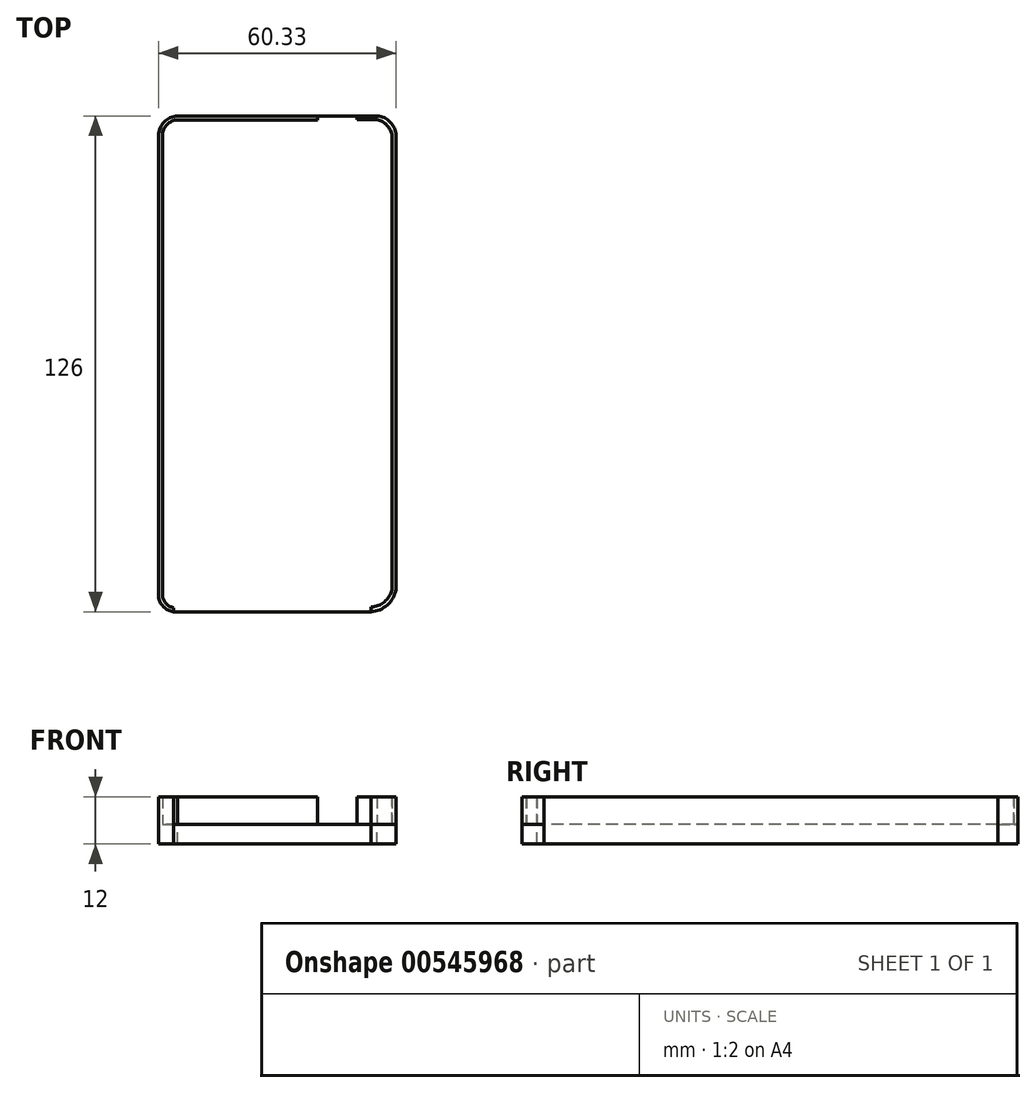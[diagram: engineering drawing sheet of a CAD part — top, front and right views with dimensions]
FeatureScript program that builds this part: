
annotation { "Feature Type Name" : "Feature", "Feature Type Description" : "" }
export const myFeature = defineFeature(function(context is Context, id is Id, definition is map)
    precondition{}
    {
        {
            var Q0;
            Q0=qCreatedBy(makeId("Top.planeOp"),FACE);
            var sketch = newSketch(context, id + "F0", { "sketchPlane" : qUnion([Q0])});
            skLineSegment(sketch, "E0.bottom", {"start": v(-22.18, 65.1) * mm, "end": v(38.15, 65.1) * mm});
            skLineSegment(sketch, "E0.top", {"start": v(-22.18, -60.9) * mm, "end": v(38.15, -60.9) * mm});
            skLineSegment(sketch, "E0.left", {"start": v(-22.18, 65.1) * mm, "end": v(-22.18, -60.9) * mm});
            skLineSegment(sketch, "E0.right", {"start": v(38.15, 65.1) * mm, "end": v(38.15, -60.9) * mm});
            skSolve(sketch);
        }
        {
            var Q0;
            Q0=makeQuery(id+"F0.imprint","IMPRINT",FACE,{"disambiguationData":[TD([[makeQuery(id+"F0.imprint","IMPRINT",EDGE,{"derivedFrom":sQuery(id+"F0.wireOp",EDGE,"E0.bottom")}),-1.0]])]});
            extrude(context, id + "F1", {"entities" : qUnion([Q0]), "depth" : 5 * mm, "offsetDistance" : 25 * mm});
        }
        {
            var Q0;
            Q0=makeQuery(id+"F1.opExtrude","CAP_FACE",FACE,{"disambiguationData":[OSD([sQuery(id+"F0.wireOp",EDGE,"E0.bottom"),sQuery(id+"F0.wireOp",EDGE,"E0.top"),sQuery(id+"F0.wireOp",EDGE,"E0.left"),sQuery(id+"F0.wireOp",EDGE,"E0.right")])],"isStart":false});
            var sketch = newSketch(context, id + "F2", { "sketchPlane" : qUnion([Q0])});
            skArc(sketch, "E1", {"start": v(-16.92, 65.1) * mm, "mid": v(-20.66, 63.66) * mm, "end": v(-22.18, 59.96) * mm});
            skArc(sketch, "E2", {"start": v(38.15, 60.04) * mm, "mid": v(36.42, 63.78) * mm, "end": v(32.51, 65.1) * mm});
            skArc(sketch, "E3", {"start": v(30.96, -60.9) * mm, "mid": v(35.63, -59.44) * mm, "end": v(38.15, -55.26) * mm});
            skArc(sketch, "E4", {"start": v(-22.18, -55.91) * mm, "mid": v(-20.88, -59.66) * mm, "end": v(-17.11, -60.9) * mm});
            skSolve(sketch);
        }
        {
            var Q0;
            {var subQ0=sQuery(id+"F2.wireOp",EDGE,"E4");var subQ1=makeQuery(id+"F1.opExtrude","CAP_EDGE",EDGE,{"disambiguationData":[OSD([sQuery(id+"F0.wireOp",EDGE,"E0.left")])],"isStart":false});var subQ2=makeQuery(id+"F2.imprint","INTERSECT",VERTEX,{"disambiguationData":[OD(1.0)],"derivedFrom":[subQ1,subQ0]});Q0=makeQuery(id+"F2.imprint","IMPRINT",FACE,{"disambiguationData":[TD([[makeQuery(id+"F2.imprint","IMPRINT",EDGE,{"disambiguationData":[TD([[subQ2,-1.0]])],"derivedFrom":subQ0}),-1.0]])]});}
            var Q1;
            {var subQ0=sQuery(id+"F2.wireOp",EDGE,"E3");var subQ1=makeQuery(id+"F1.opExtrude","CAP_EDGE",EDGE,{"disambiguationData":[OSD([sQuery(id+"F0.wireOp",EDGE,"E0.right")])],"isStart":false});var subQ2=makeQuery(id+"F2.imprint","INTERSECT",VERTEX,{"derivedFrom":[subQ1,subQ0]});Q1=makeQuery(id+"F2.imprint","IMPRINT",FACE,{"disambiguationData":[TD([[makeQuery(id+"F2.imprint","IMPRINT",EDGE,{"disambiguationData":[TD([[subQ2,1.0]])],"derivedFrom":subQ0}),-1.0]])]});}
            var Q2;
            {var subQ0=sQuery(id+"F2.wireOp",EDGE,"E2");var subQ1=makeQuery(id+"F1.opExtrude","CAP_EDGE",EDGE,{"disambiguationData":[OSD([sQuery(id+"F0.wireOp",EDGE,"E0.right")])],"isStart":false});var subQ2=makeQuery(id+"F2.imprint","INTERSECT",VERTEX,{"derivedFrom":[subQ1,subQ0]});Q2=makeQuery(id+"F2.imprint","IMPRINT",FACE,{"disambiguationData":[TD([[makeQuery(id+"F2.imprint","IMPRINT",EDGE,{"disambiguationData":[TD([[subQ2,-1.0]])],"derivedFrom":subQ0}),-1.0]])]});}
            var Q3;
            {var subQ0=sQuery(id+"F2.wireOp",EDGE,"E1");var subQ1=makeQuery(id+"F1.opExtrude","CAP_EDGE",EDGE,{"disambiguationData":[OSD([sQuery(id+"F0.wireOp",EDGE,"E0.bottom")])],"isStart":false});var subQ2=makeQuery(id+"F2.imprint","INTERSECT",VERTEX,{"disambiguationData":[OD(1.0)],"derivedFrom":[subQ1,subQ0]});Q3=makeQuery(id+"F2.imprint","IMPRINT",FACE,{"disambiguationData":[TD([[makeQuery(id+"F2.imprint","IMPRINT",EDGE,{"disambiguationData":[TD([[subQ2,-1.0]])],"derivedFrom":subQ0}),-1.0]])]});}
            extrude(context, id + "F3", {"entities" : qUnion([Q0, Q1, Q2, Q3]), "operationType" : NewBodyOperationType.REMOVE, "oppositeDirection" : true, "depth" : 25 * mm, "offsetDistance" : 25 * mm});
        }
        {
            var Q0;
            Q0=makeQuery(id+"F1.opExtrude","CAP_FACE",FACE,{"disambiguationData":[OSD([sQuery(id+"F0.wireOp",EDGE,"E0.bottom"),sQuery(id+"F0.wireOp",EDGE,"E0.top"),sQuery(id+"F0.wireOp",EDGE,"E0.left"),sQuery(id+"F0.wireOp",EDGE,"E0.right")])],"isStart":false});
            var sketch = newSketch(context, id + "F4", { "sketchPlane" : qUnion([Q0])});
            skLineSegment(sketch, "E5.bottom", {"start": v(-22.18, 60.13) * mm, "end": v(-21.18, 60.13) * mm});
            skLineSegment(sketch, "E5.top", {"start": v(-22.18, -57.05) * mm, "end": v(-21.18, -57.05) * mm});
            skLineSegment(sketch, "E5.left", {"start": v(-22.18, 60.13) * mm, "end": v(-22.18, -57.05) * mm});
            skLineSegment(sketch, "E5.right", {"start": v(-21.18, 60.13) * mm, "end": v(-21.18, -57.05) * mm});
            skLineSegment(sketch, "E6.bottom", {"start": v(38.15, 60.04) * mm, "end": v(37.15, 60.04) * mm});
            skLineSegment(sketch, "E6.top", {"start": v(38.15, -55.26) * mm, "end": v(37.15, -55.26) * mm});
            skLineSegment(sketch, "E6.left", {"start": v(38.15, 60.04) * mm, "end": v(38.15, -55.26) * mm});
            skLineSegment(sketch, "E6.right", {"start": v(37.15, 60.04) * mm, "end": v(37.15, -55.26) * mm});
            skSolve(sketch);
        }
        {
            var Q0;
            Q0=makeQuery(id+"F1.opExtrude","CAP_FACE",FACE,{"disambiguationData":[OSD([sQuery(id+"F0.wireOp",EDGE,"E0.bottom"),sQuery(id+"F0.wireOp",EDGE,"E0.top"),sQuery(id+"F0.wireOp",EDGE,"E0.left"),sQuery(id+"F0.wireOp",EDGE,"E0.right")])],"isStart":false});
            var sketch = newSketch(context, id + "F5", { "sketchPlane" : qUnion([Q0])});
            skArc(sketch, "E7", {"start": v(-22.18, -57.05) * mm, "mid": v(-20.94, -59.61) * mm, "end": v(-18.4, -60.9) * mm});
            skArc(sketch, "E8", {"start": v(-21.18, -57.05) * mm, "mid": v(-20.2, -58.87) * mm, "end": v(-18.4, -59.87) * mm});
            skLineSegment(sketch, "E9", {"start": v(-22.18, -57.05) * mm, "end": v(-21.18, -57.05) * mm});
            skLineSegment(sketch, "E10", {"start": v(-18.4, -59.87) * mm, "end": v(-18.4, -60.9) * mm});
            skSolve(sketch);
        }
        {
            var Q0;
            Q0=makeQuery(id+"F5.imprint","IMPRINT",FACE,{"disambiguationData":[TD([[makeQuery(id+"F5.imprint","IMPRINT",EDGE,{"derivedFrom":sQuery(id+"F5.wireOp",EDGE,"E8")}),-1.0]])]});
            extrude(context, id + "F6", {"entities" : qUnion([Q0]), "operationType" : NewBodyOperationType.ADD, "depth" : 7 * mm, "offsetDistance" : 25 * mm});
        }
        {
            var Q0;
            Q0=makeQuery(id+"F1.opExtrude","CAP_FACE",FACE,{"disambiguationData":[OSD([sQuery(id+"F0.wireOp",EDGE,"E0.bottom"),sQuery(id+"F0.wireOp",EDGE,"E0.top"),sQuery(id+"F0.wireOp",EDGE,"E0.left"),sQuery(id+"F0.wireOp",EDGE,"E0.right")])],"isStart":false});
            var sketch = newSketch(context, id + "F7", { "sketchPlane" : qUnion([Q0])});
            skArc(sketch, "E11", {"start": v(-17.3, 65.1) * mm, "mid": v(-20.73, 63.58) * mm, "end": v(-22.18, 60.13) * mm});
            skArc(sketch, "E12", {"start": v(-17.3, 64.1) * mm, "mid": v(-20.05, 62.9) * mm, "end": v(-21.18, 60.13) * mm});
            skLineSegment(sketch, "E13", {"start": v(-17.3, 65.1) * mm, "end": v(-17.3, 64.1) * mm});
            skLineSegment(sketch, "E14", {"start": v(-21.18, 60.13) * mm, "end": v(-22.18, 60.13) * mm});
            skSolve(sketch);
        }
        {
            var Q0;
            Q0=makeQuery(id+"F7.imprint","IMPRINT",FACE,{"disambiguationData":[TD([[makeQuery(id+"F7.imprint","IMPRINT",EDGE,{"derivedFrom":sQuery(id+"F7.wireOp",EDGE,"E11")}),1.0]])]});
            extrude(context, id + "F8", {"entities" : qUnion([Q0]), "operationType" : NewBodyOperationType.ADD, "depth" : 7 * mm, "offsetDistance" : 25 * mm});
        }
        {
            var Q0;
            Q0=makeQuery(id+"F1.opExtrude","CAP_FACE",FACE,{"disambiguationData":[OSD([sQuery(id+"F0.wireOp",EDGE,"E0.bottom"),sQuery(id+"F0.wireOp",EDGE,"E0.top"),sQuery(id+"F0.wireOp",EDGE,"E0.left"),sQuery(id+"F0.wireOp",EDGE,"E0.right")])],"isStart":false});
            var sketch = newSketch(context, id + "F9", { "sketchPlane" : qUnion([Q0])});
            skLineSegment(sketch, "E15.bottom", {"start": v(33.35, 65.1) * mm, "end": v(28.23, 65.1) * mm});
            skLineSegment(sketch, "E15.top", {"start": v(33.35, 64.1) * mm, "end": v(28.23, 64.1) * mm});
            skLineSegment(sketch, "E15.left", {"start": v(33.35, 65.1) * mm, "end": v(33.35, 64.1) * mm});
            skLineSegment(sketch, "E15.right", {"start": v(28.23, 65.1) * mm, "end": v(28.23, 64.1) * mm});
            skSolve(sketch);
        }
        {
            var Q0;
            Q0=makeQuery(id+"F9.imprint","IMPRINT",FACE,{"disambiguationData":[TD([[makeQuery(id+"F9.imprint","IMPRINT",EDGE,{"derivedFrom":sQuery(id+"F9.wireOp",EDGE,"E15.bottom")}),-1.0]])]});
            extrude(context, id + "F10", {"entities" : qUnion([Q0]), "operationType" : NewBodyOperationType.ADD, "depth" : 7 * mm, "offsetDistance" : 25 * mm});
        }
        {
            var Q0;
            Q0=makeQuery(id+"F1.opExtrude","CAP_FACE",FACE,{"disambiguationData":[OSD([sQuery(id+"F0.wireOp",EDGE,"E0.bottom"),sQuery(id+"F0.wireOp",EDGE,"E0.top"),sQuery(id+"F0.wireOp",EDGE,"E0.left"),sQuery(id+"F0.wireOp",EDGE,"E0.right")])],"isStart":false});
            var sketch = newSketch(context, id + "F11", { "sketchPlane" : qUnion([Q0])});
            skLineSegment(sketch, "E16", {"start": v(28.23, 65.1) * mm, "end": v(18.23, 65.1) * mm});
            skSolve(sketch);
        }
        {
            var Q0;
            {var subQ1=sQuery(id+"F11.wireOp",EDGE,"E16");Q0=makeQuery(id+"F11.imprint","IMPRINT",FACE,{"disambiguationData":[TD([[makeQuery(id+"F11.imprint","IMPRINT",EDGE,{"derivedFrom":subQ1}),-1.0]])]});}
            var sketch = newSketch(context, id + "F12", { "sketchPlane" : qUnion([Q0])});
            skLineSegment(sketch, "E17.bottom", {"start": v(-17.3, 64.1) * mm, "end": v(18.23, 64.1) * mm});
            skLineSegment(sketch, "E17.top", {"start": v(-17.3, 65.1) * mm, "end": v(18.23, 65.1) * mm});
            skLineSegment(sketch, "E17.left", {"start": v(-17.3, 64.1) * mm, "end": v(-17.3, 65.1) * mm});
            skLineSegment(sketch, "E17.right", {"start": v(18.23, 64.1) * mm, "end": v(18.23, 65.1) * mm});
            skSolve(sketch);
        }
        {
            var Q0;
            Q0=makeQuery(id+"F12.imprint","IMPRINT",FACE,{"disambiguationData":[TD([[makeQuery(id+"F12.imprint","IMPRINT",EDGE,{"derivedFrom":sQuery(id+"F12.wireOp",EDGE,"E17.bottom")}),1.0]])]});
            extrude(context, id + "F13", {"entities" : qUnion([Q0]), "operationType" : NewBodyOperationType.ADD, "depth" : 7 * mm, "offsetDistance" : 25 * mm});
        }
        {
            var Q0;
            Q0 = qSketchRegion(id + "F4", true);
            extrude(context, id + "F14", {"entities" : qUnion([Q0]), "operationType" : NewBodyOperationType.ADD, "depth" : 7 * mm, "offsetDistance" : 25 * mm});
        }
        {
            var Q0;
            {var subQ0=sQuery(id+"F11.wireOp",EDGE,"E16");Q0=makeQuery(id+"F11.imprint","IMPRINT",FACE,{"disambiguationData":[TD([[makeQuery(id+"F11.imprint","IMPRINT",EDGE,{"derivedFrom":subQ0}),-1.0]])]});}
            var sketch = newSketch(context, id + "F15", { "sketchPlane" : qUnion([Q0])});
            skArc(sketch, "E18", {"start": v(38.15, 60.04) * mm, "mid": v(36.72, 63.5) * mm, "end": v(33.35, 65.1) * mm});
            skArc(sketch, "E19", {"start": v(37.15, 60.04) * mm, "mid": v(35.92, 62.7) * mm, "end": v(33.35, 64.1) * mm});
            skLineSegment(sketch, "E20", {"start": v(33.35, 65.1) * mm, "end": v(33.35, 64.1) * mm});
            skLineSegment(sketch, "E21", {"start": v(37.15, 60.04) * mm, "end": v(38.15, 60.04) * mm});
            skSolve(sketch);
        }
        {
            var Q0;
            Q0 = qSketchRegion(id + "F15", true);
            extrude(context, id + "F16", {"entities" : qUnion([Q0]), "operationType" : NewBodyOperationType.ADD, "depth" : 7 * mm, "offsetDistance" : 25 * mm});
        }
        {
            var Q0;
            {var subQ0=sQuery(id+"F11.wireOp",EDGE,"E16");Q0=makeQuery(id+"F11.imprint","IMPRINT",FACE,{"disambiguationData":[TD([[makeQuery(id+"F11.imprint","IMPRINT",EDGE,{"derivedFrom":subQ0}),-1.0]])]});}
            var sketch = newSketch(context, id + "F17", { "sketchPlane" : qUnion([Q0])});
            skArc(sketch, "E22", {"start": v(31.8, -60.9) * mm, "mid": v(35.94, -59.17) * mm, "end": v(38.15, -55.26) * mm});
            skArc(sketch, "E23", {"start": v(31.8, -59.7) * mm, "mid": v(35.2, -58.35) * mm, "end": v(37.14, -55.23) * mm});
            skLineSegment(sketch, "E24", {"start": v(31.8, -59.7) * mm, "end": v(31.8, -60.9) * mm});
            skLineSegment(sketch, "E25", {"start": v(37.14, -55.23) * mm, "end": v(38.15, -55.26) * mm});
            skSolve(sketch);
        }
        {
            var Q0;
            Q0 = qSketchRegion(id + "F17", true);
            extrude(context, id + "F18", {"entities" : qUnion([Q0]), "operationType" : NewBodyOperationType.ADD, "depth" : 7 * mm, "offsetDistance" : 25 * mm});
        }
    });
